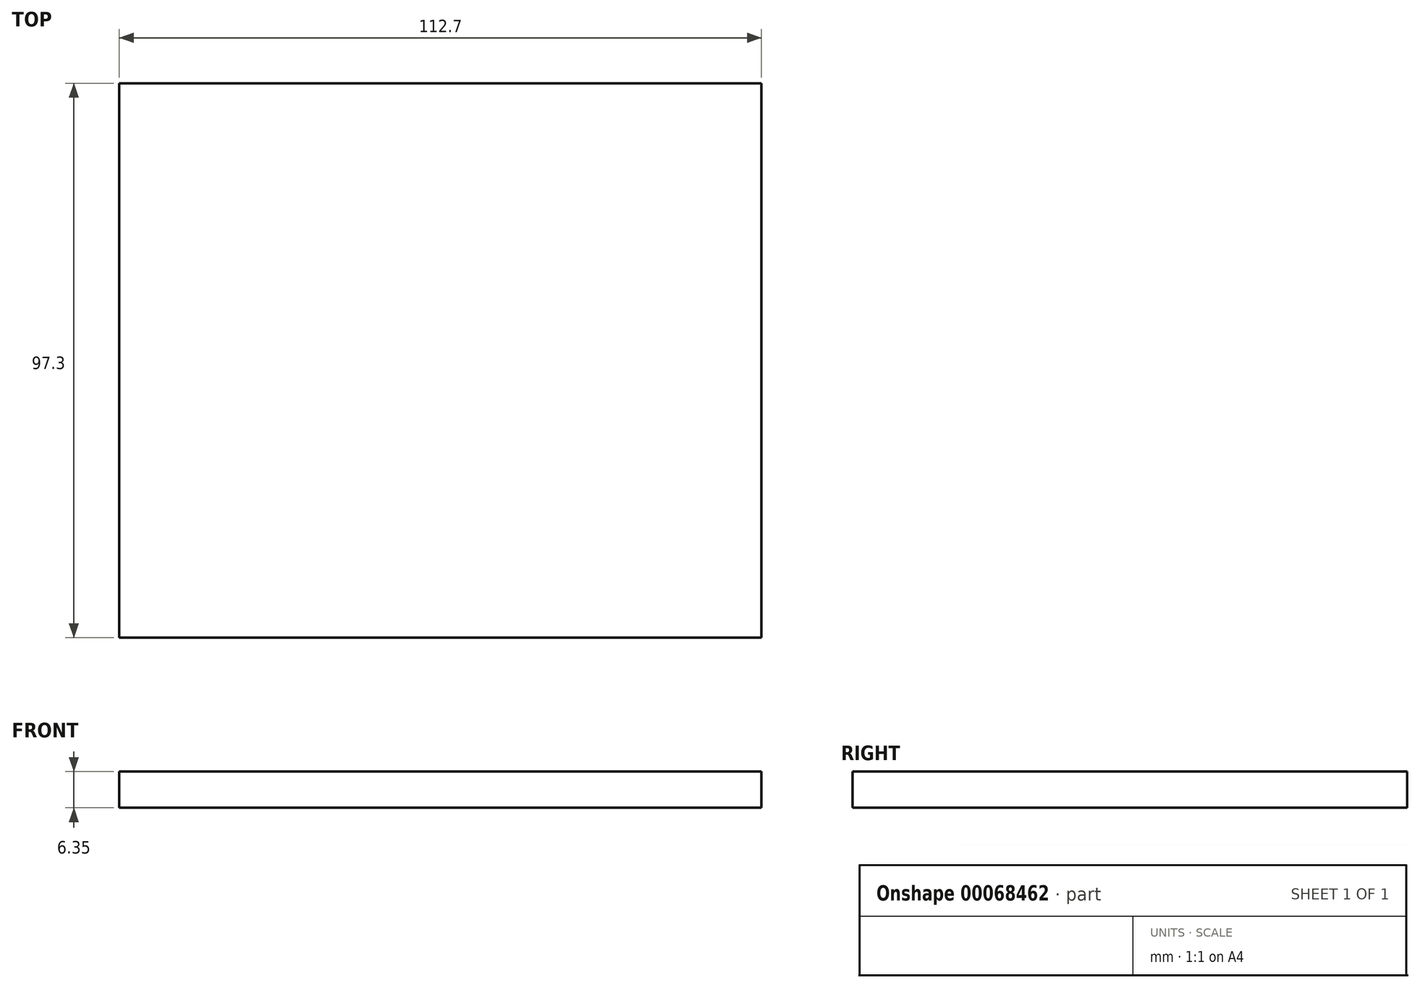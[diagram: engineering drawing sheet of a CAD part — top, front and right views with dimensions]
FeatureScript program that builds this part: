
annotation { "Feature Type Name" : "Feature", "Feature Type Description" : "" }
export const myFeature = defineFeature(function(context is Context, id is Id, definition is map)
    precondition{}
    {
        {
            var Q0;
            Q0=qCreatedBy(makeId("Top.planeOp"),FACE);
            var sketch = newSketch(context, id + "F0", { "sketchPlane" : qUnion([Q0])});
            skLineSegment(sketch, "E0.rect.bottom", {"start": v(56.35, 48.65) * mm, "end": v(-56.35, 48.65) * mm});
            skLineSegment(sketch, "E0.rect.top", {"start": v(56.35, -48.65) * mm, "end": v(-56.35, -48.65) * mm});
            skLineSegment(sketch, "E0.rect.left", {"start": v(56.35, 48.65) * mm, "end": v(56.35, -48.65) * mm});
            skLineSegment(sketch, "E0.rect.right", {"start": v(-56.35, 48.65) * mm, "end": v(-56.35, -48.65) * mm});
            skPoint(sketch, "E0.rect.middle", {"position": v(0, 0) * mm});
            skSolve(sketch);
        }
        {
            var Q0;
            Q0 = qSketchRegion(id + "F0", true);
            extrude(context, id + "F1", {"entities" : qUnion([Q0]), "depth" : 6.35 * mm});
        }
    });
